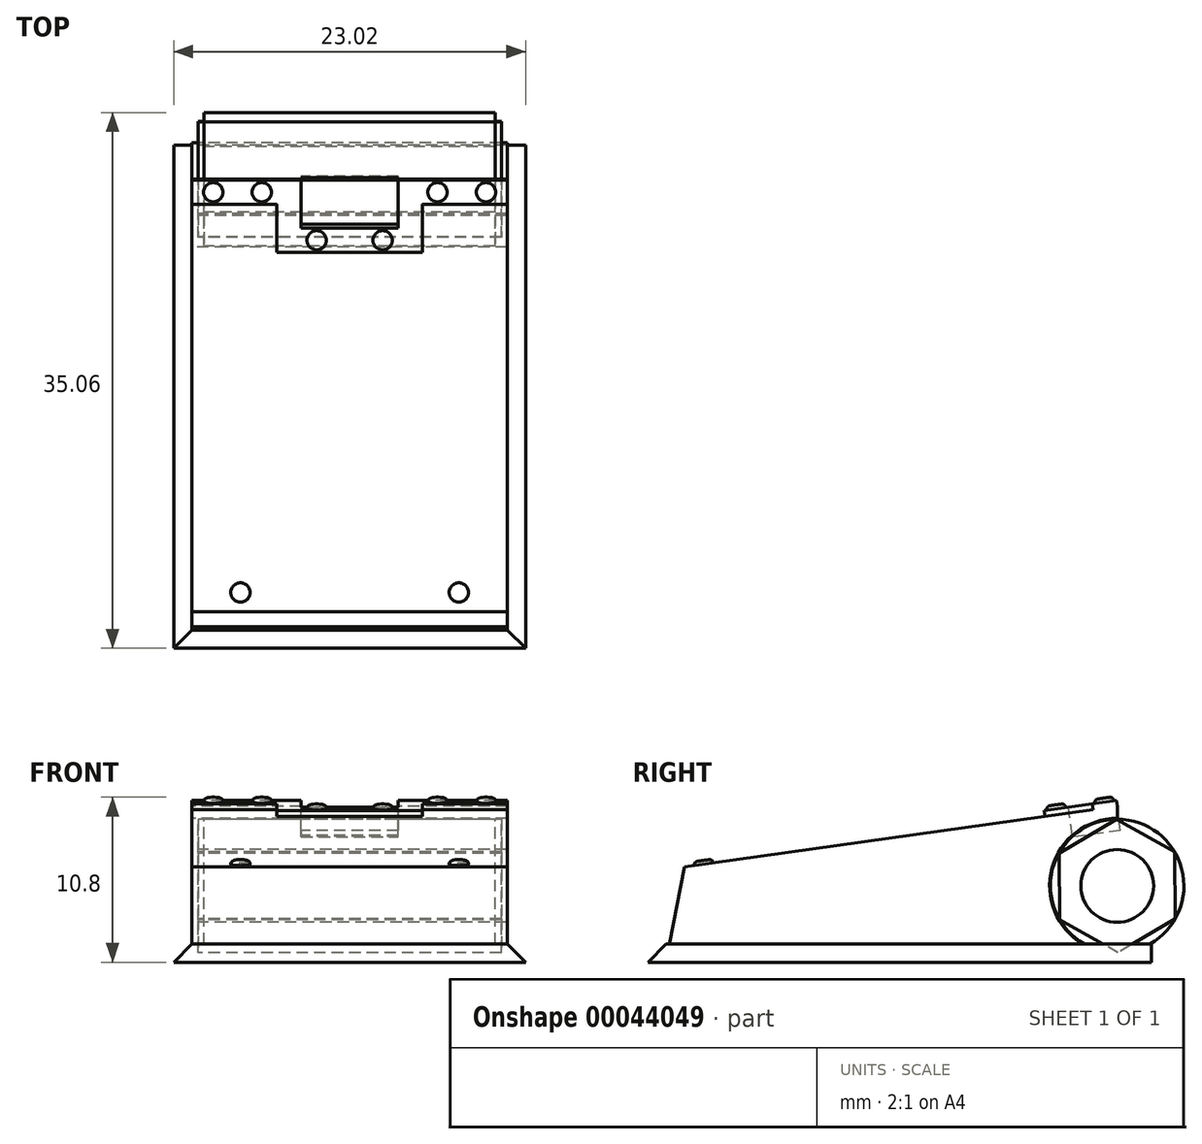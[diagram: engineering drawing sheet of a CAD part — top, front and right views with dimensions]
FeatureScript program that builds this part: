
annotation { "Feature Type Name" : "Feature", "Feature Type Description" : "" }
export const myFeature = defineFeature(function(context is Context, id is Id, definition is map)
    precondition{}
    {
        {
            var Q0;
            Q0=qCreatedBy(makeId("Right.planeOp"),FACE);
            var sketch = newSketch(context, id + "F0", { "sketchPlane" : qUnion([Q0])});
            skLineSegment(sketch, "E0", {"start": v(0, 0) * mm, "end": v(-31.75, 0) * mm});
            skLineSegment(sketch, "E1", {"start": v(-31.75, 0) * mm, "end": v(-30.54, 6.23) * mm});
            skLineSegment(sketch, "E2", {"start": v(-30.54, 6.23) * mm, "end": v(-2.24, 10.21) * mm});
            skCircle(sketch, "E3", {"center": v(-2.24, 5) * mm, "radius": 4.42 * mm});
            skLineSegment(sketch, "E4", {"start": v(-2.24, 10.21) * mm, "end": v(-2.24, 9.42) * mm});
            skLineSegment(sketch, "E5", {"start": v(0, 0) * mm, "end": v(0, 1.2) * mm});
            skSolve(sketch);
        }
        {
            var Q0;
            Q0=makeQuery(id+"F0.imprint","IMPRINT",FACE,{"disambiguationData":[TD([[makeQuery(id+"F0.imprint","IMPRINT",EDGE,{"derivedFrom":sQuery(id+"F0.wireOp",EDGE,"E0")}),-1.0]])]});
            extrude(context, id + "F1", {"entities" : qUnion([Q0]), "endBound" : BoundingType.SYMMETRIC, "depth" : 20.64 * mm});
        }
        {
            var Q0;
            Q0=qCreatedBy(makeId("Right.planeOp"),FACE);
            var sketch = newSketch(context, id + "F2", { "sketchPlane" : qUnion([Q0])});
            skCircle(sketch, "E6", {"center": v(-2.24, 5) * mm, "radius": 4.37 * mm});
            skSolve(sketch);
        }
        {
            var Q0;
            Q0 = qSketchRegion(id + "F2", true);
            extrude(context, id + "F3", {"entities" : qUnion([Q0]), "endBound" : BoundingType.SYMMETRIC, "depth" : 19.05 * mm});
        }
        {
            var Q0;
            Q0=makeQuery(id+"F1.opExtrude","SWEPT_FACE",FACE,{"disambiguationData":[OSD([sQuery(id+"F0.wireOp",EDGE,"E2")])]});
            var sketch = newSketch(context, id + "F4", { "sketchPlane" : qUnion([Q0])});
            skLineSegment(sketch, "E7", {"start": v(0, -0.8) * mm, "end": v(-3.18, -0.8) * mm});
            skLineSegment(sketch, "E8", {"start": v(-3.18, -0.8) * mm, "end": v(-3.18, -3.97) * mm});
            skLineSegment(sketch, "E9", {"start": v(-3.18, -3.97) * mm, "end": v(3.18, -3.97) * mm});
            skLineSegment(sketch, "E10", {"start": v(3.17, -3.97) * mm, "end": v(3.17, -0.8) * mm});
            skLineSegment(sketch, "E11", {"start": v(3.17, -0.8) * mm, "end": v(0, -0.8) * mm});
            skSolve(sketch);
        }
        {
            var Q0;
            Q0 = qSketchRegion(id + "F4", true);
            extrude(context, id + "F5", {"entities" : qUnion([Q0]), "operationType" : NewBodyOperationType.REMOVE, "oppositeDirection" : true, "depth" : 1.59 * mm});
        }
        {
            var Q0;
            Q0=makeQuery(id+"F1.opExtrude","SWEPT_FACE",FACE,{"disambiguationData":[OSD([sQuery(id+"F0.wireOp",EDGE,"E5")])]});
            var sketch = newSketch(context, id + "F6", { "sketchPlane" : qUnion([Q0])});
            skLineSegment(sketch, "E12", {"start": v(0, 0) * mm, "end": v(-11.51, 0) * mm});
            skLineSegment(sketch, "E13", {"start": v(11.51, 0) * mm, "end": v(0, 0) * mm});
            skLineSegment(sketch, "E14", {"start": v(0, 0) * mm, "end": v(0, 1.2) * mm});
            skLineSegment(sketch, "E15", {"start": v(-11.51, 0) * mm, "end": v(-11.51, 1.2) * mm});
            skLineSegment(sketch, "E16", {"start": v(-11.51, 1.2) * mm, "end": v(11.51, 1.2) * mm});
            skLineSegment(sketch, "E17", {"start": v(11.51, 1.2) * mm, "end": v(11.51, 0) * mm});
            skSolve(sketch);
        }
        {
            var Q0;
            Q0 = qSketchRegion(id + "F6", true);
            extrude(context, id + "F7", {"entities" : qUnion([Q0]), "operationType" : NewBodyOperationType.ADD, "oppositeDirection" : true, "depth" : 32.94 * mm});
        }
        {
            var Q0;
            Q0=makeQuery(id+"F7.opExtrude","SWEPT_EDGE",EDGE,{"disambiguationData":[OSD([sQuery(id+"F6.wireOp",EDGE,"E15"),sQuery(id+"F6.wireOp",EDGE,"E16")])]});
            var Q1;
            Q1=makeQuery(id+"F7.opExtrude","CAP_EDGE",EDGE,{"disambiguationData":[OSD([sQuery(id+"F6.wireOp",EDGE,"E16")])],"isStart":false});
            var Q2;
            Q2=makeQuery(id+"F7.opExtrude","SWEPT_EDGE",EDGE,{"disambiguationData":[OSD([sQuery(id+"F6.wireOp",EDGE,"E16"),sQuery(id+"F6.wireOp",EDGE,"E17")])]});
            chamfer(context, id + "F8", {"entities" : qUnion([Q0, Q1, Q2]), "width" : 1.2 * mm, "tangentPropagation" : true});
        }
        {
            var Q0;
            Q0=makeQuery(id+"F3.opExtrude","CAP_FACE",FACE,{"disambiguationData":[OSD([sQuery(id+"F2.wireOp",EDGE,"E6")])],"isStart":false});
            var sketch = newSketch(context, id + "F9", { "sketchPlane" : qUnion([Q0])});
            skCircle(sketch, "E18.cCircle", {"center": v(-2.24, 5) * mm, "radius": 4.37 * mm, "construction": true});
            skLineSegment(sketch, "E18.0", {"start": v(-2.3, 9.36) * mm, "end": v(1.51, 7.23) * mm});
            skLineSegment(sketch, "E18.1", {"start": v(1.51, 7.23) * mm, "end": v(1.57, 2.86) * mm});
            skLineSegment(sketch, "E18.2", {"start": v(1.57, 2.86) * mm, "end": v(-2.19, 0.63) * mm});
            skLineSegment(sketch, "E18.3", {"start": v(-2.19, 0.63) * mm, "end": v(-6, 2.77) * mm});
            skLineSegment(sketch, "E18.4", {"start": v(-6, 2.77) * mm, "end": v(-6.05, 7.14) * mm});
            skLineSegment(sketch, "E18.5", {"start": v(-6.05, 7.14) * mm, "end": v(-2.3, 9.36) * mm});
            skSolve(sketch);
        }
        {
            var Q0;
            Q0 = qSketchRegion(id + "F9", true);
            extrude(context, id + "F10", {"entities" : qUnion([Q0]), "depth" : 0.4 * mm, "hasSecondDirection" : true, "secondDirectionOppositeDirection" : true, "secondDirectionDepth" : 19.45 * mm});
        }
        {
            var Q0;
            Q0=makeQuery(id+"F10.opExtrude","CAP_FACE",FACE,{"disambiguationData":[OSD([sQuery(id+"F9.wireOp",EDGE,"E18.0"),sQuery(id+"F9.wireOp",EDGE,"E18.1"),sQuery(id+"F9.wireOp",EDGE,"E18.2"),sQuery(id+"F9.wireOp",EDGE,"E18.3"),sQuery(id+"F9.wireOp",EDGE,"E18.4"),sQuery(id+"F9.wireOp",EDGE,"E18.5")])],"isStart":false});
            var sketch = newSketch(context, id + "F11", { "sketchPlane" : qUnion([Q0])});
            skSolve(sketch);
        }
        {
            var Q0;
            Q0=makeQuery(id+"F11.imprint","IMPRINT",FACE,{"disambiguationData":[TD([[makeQuery(id+"F11.imprint","IMPRINT",EDGE,{"derivedFrom":makeQuery(id+"F10.opExtrude","CAP_EDGE",EDGE,{"disambiguationData":[OSD([sQuery(id+"F9.wireOp",EDGE,"E18.0")])],"isStart":false})}),-1.0]])]});
            var sketch = newSketch(context, id + "F12", { "sketchPlane" : qUnion([Q0])});
            skCircle(sketch, "E19", {"center": v(-2.24, 5) * mm, "radius": 2.38 * mm});
            skSolve(sketch);
        }
        {
            var Q0;
            Q0 = qSketchRegion(id + "F12", true);
            extrude(context, id + "F13", {"entities" : qUnion([Q0]), "depth" : 0.4 * mm, "hasSecondDirection" : true, "secondDirectionOppositeDirection" : true, "secondDirectionDepth" : 20.24 * mm});
        }
        {
            var Q0;
            Q0=makeQuery(id+"F1.opExtrude","SWEPT_FACE",FACE,{"disambiguationData":[OSD([sQuery(id+"F0.wireOp",EDGE,"E2")])]});
            var sketch = newSketch(context, id + "F14", { "sketchPlane" : qUnion([Q0])});
            skLineSegment(sketch, "E20", {"start": v(-10.32, -0.8) * mm, "end": v(-10.32, -2.39) * mm});
            skLineSegment(sketch, "E21", {"start": v(-10.32, -2.39) * mm, "end": v(-4.76, -2.39) * mm});
            skLineSegment(sketch, "E22", {"start": v(-4.76, -2.39) * mm, "end": v(-4.76, -5.56) * mm});
            skLineSegment(sketch, "E23", {"start": v(-4.76, -5.56) * mm, "end": v(4.76, -5.56) * mm});
            skLineSegment(sketch, "E24", {"start": v(4.76, -5.56) * mm, "end": v(4.76, -2.39) * mm});
            skLineSegment(sketch, "E25", {"start": v(4.76, -2.39) * mm, "end": v(10.32, -2.39) * mm});
            skLineSegment(sketch, "E26", {"start": v(10.32, -2.39) * mm, "end": v(10.32, -0.8) * mm});
            skLineSegment(sketch, "E27", {"start": v(10.32, -0.8) * mm, "end": v(3.18, -0.8) * mm});
            skLineSegment(sketch, "E28", {"start": v(3.18, -0.8) * mm, "end": v(3.18, -3.97) * mm});
            skLineSegment(sketch, "E29", {"start": v(3.18, -3.97) * mm, "end": v(-3.18, -3.97) * mm});
            skLineSegment(sketch, "E30", {"start": v(-3.18, -3.97) * mm, "end": v(-3.18, -0.8) * mm});
            skLineSegment(sketch, "E31", {"start": v(-3.18, -0.8) * mm, "end": v(-10.32, -0.8) * mm});
            skSolve(sketch);
        }
        {
            var Q0;
            Q0 = qSketchRegion(id + "F14", true);
            extrude(context, id + "F15", {"entities" : qUnion([Q0]), "operationType" : NewBodyOperationType.ADD, "depth" : 0.4 * mm});
        }
        {
            var Q0;
            Q0=makeQuery(id+"F1.opExtrude","SWEPT_FACE",FACE,{"disambiguationData":[OSD([sQuery(id+"F0.wireOp",EDGE,"E2")])]});
            var sketch = newSketch(context, id + "F16", { "sketchPlane" : qUnion([Q0])});
            skCircle(sketch, "E32", {"center": v(-7.14, -28.1) * mm, "radius": 0.64 * mm});
            skCircle(sketch, "E33", {"center": v(7.14, -28.1) * mm, "radius": 0.64 * mm});
            skSolve(sketch);
        }
        {
            var Q0;
            Q0 = qSketchRegion(id + "F16", true);
            extrude(context, id + "F17", {"entities" : qUnion([Q0]), "operationType" : NewBodyOperationType.ADD, "depth" : 0.25 * mm});
        }
        {
            var Q0;
            Q0=makeQuery(id+"F17.opExtrude","CAP_EDGE",EDGE,{"disambiguationData":[OSD([sQuery(id+"F16.wireOp",EDGE,"E32")])],"isStart":false});
            var Q1;
            Q1=makeQuery(id+"F17.opExtrude","CAP_FACE",FACE,{"disambiguationData":[OSD([sQuery(id+"F16.wireOp",EDGE,"E33")])],"isStart":false});
            fillet(context, id + "F18", {"entities" : qUnion([Q0, Q1]), "radius" : 0.25 * mm, "tangentPropagation" : true, "allowEdgeOverflow" : false});
        }
        {
            var Q0;
            Q0=makeQuery(id+"F15.opExtrude","CAP_FACE",FACE,{"disambiguationData":[OSD([sQuery(id+"F14.wireOp",EDGE,"E20"),sQuery(id+"F14.wireOp",EDGE,"E21"),sQuery(id+"F14.wireOp",EDGE,"E22"),sQuery(id+"F14.wireOp",EDGE,"E23"),sQuery(id+"F14.wireOp",EDGE,"E24"),sQuery(id+"F14.wireOp",EDGE,"E25"),sQuery(id+"F14.wireOp",EDGE,"E26"),sQuery(id+"F14.wireOp",EDGE,"E27"),sQuery(id+"F14.wireOp",EDGE,"E28"),sQuery(id+"F14.wireOp",EDGE,"E29"),sQuery(id+"F14.wireOp",EDGE,"E30"),sQuery(id+"F14.wireOp",EDGE,"E31")])],"isStart":false});
            var sketch = newSketch(context, id + "F19", { "sketchPlane" : qUnion([Q0])});
            skCircle(sketch, "E34", {"center": v(-8.92, -1.6) * mm, "radius": 0.64 * mm});
            skCircle(sketch, "E35", {"center": v(-5.75, -1.6) * mm, "radius": 0.64 * mm});
            skCircle(sketch, "E36", {"center": v(-2.16, -4.77) * mm, "radius": 0.64 * mm});
            skCircle(sketch, "E37", {"center": v(2.16, -4.77) * mm, "radius": 0.64 * mm});
            skCircle(sketch, "E38", {"center": v(5.75, -1.6) * mm, "radius": 0.64 * mm});
            skCircle(sketch, "E39", {"center": v(8.92, -1.6) * mm, "radius": 0.64 * mm});
            skSolve(sketch);
        }
        {
            var Q0;
            Q0 = qSketchRegion(id + "F19", true);
            extrude(context, id + "F20", {"entities" : qUnion([Q0]), "operationType" : NewBodyOperationType.ADD, "depth" : 0.25 * mm});
        }
        {
            var Q0;
            Q0=makeQuery(id+"F20.opExtrude","CAP_EDGE",EDGE,{"disambiguationData":[OSD([sQuery(id+"F19.wireOp",EDGE,"E34")])],"isStart":false});
            var Q1;
            Q1=makeQuery(id+"F20.opExtrude","CAP_EDGE",EDGE,{"disambiguationData":[OSD([sQuery(id+"F19.wireOp",EDGE,"E35")])],"isStart":false});
            var Q2;
            Q2=makeQuery(id+"F20.opExtrude","CAP_EDGE",EDGE,{"disambiguationData":[OSD([sQuery(id+"F19.wireOp",EDGE,"E36")])],"isStart":false});
            var Q3;
            Q3=makeQuery(id+"F20.opExtrude","CAP_FACE",FACE,{"disambiguationData":[OSD([sQuery(id+"F19.wireOp",EDGE,"E37")])],"isStart":false});
            var Q4;
            Q4=makeQuery(id+"F20.opExtrude","CAP_FACE",FACE,{"disambiguationData":[OSD([sQuery(id+"F19.wireOp",EDGE,"E38")])],"isStart":false});
            var Q5;
            Q5=makeQuery(id+"F20.opExtrude","CAP_FACE",FACE,{"disambiguationData":[OSD([sQuery(id+"F19.wireOp",EDGE,"E39")])],"isStart":false});
            fillet(context, id + "F21", {"entities" : qUnion([Q0, Q1, Q2, Q3, Q4, Q5]), "radius" : 0.25 * mm, "tangentPropagation" : true, "allowEdgeOverflow" : false});
        }
    });
